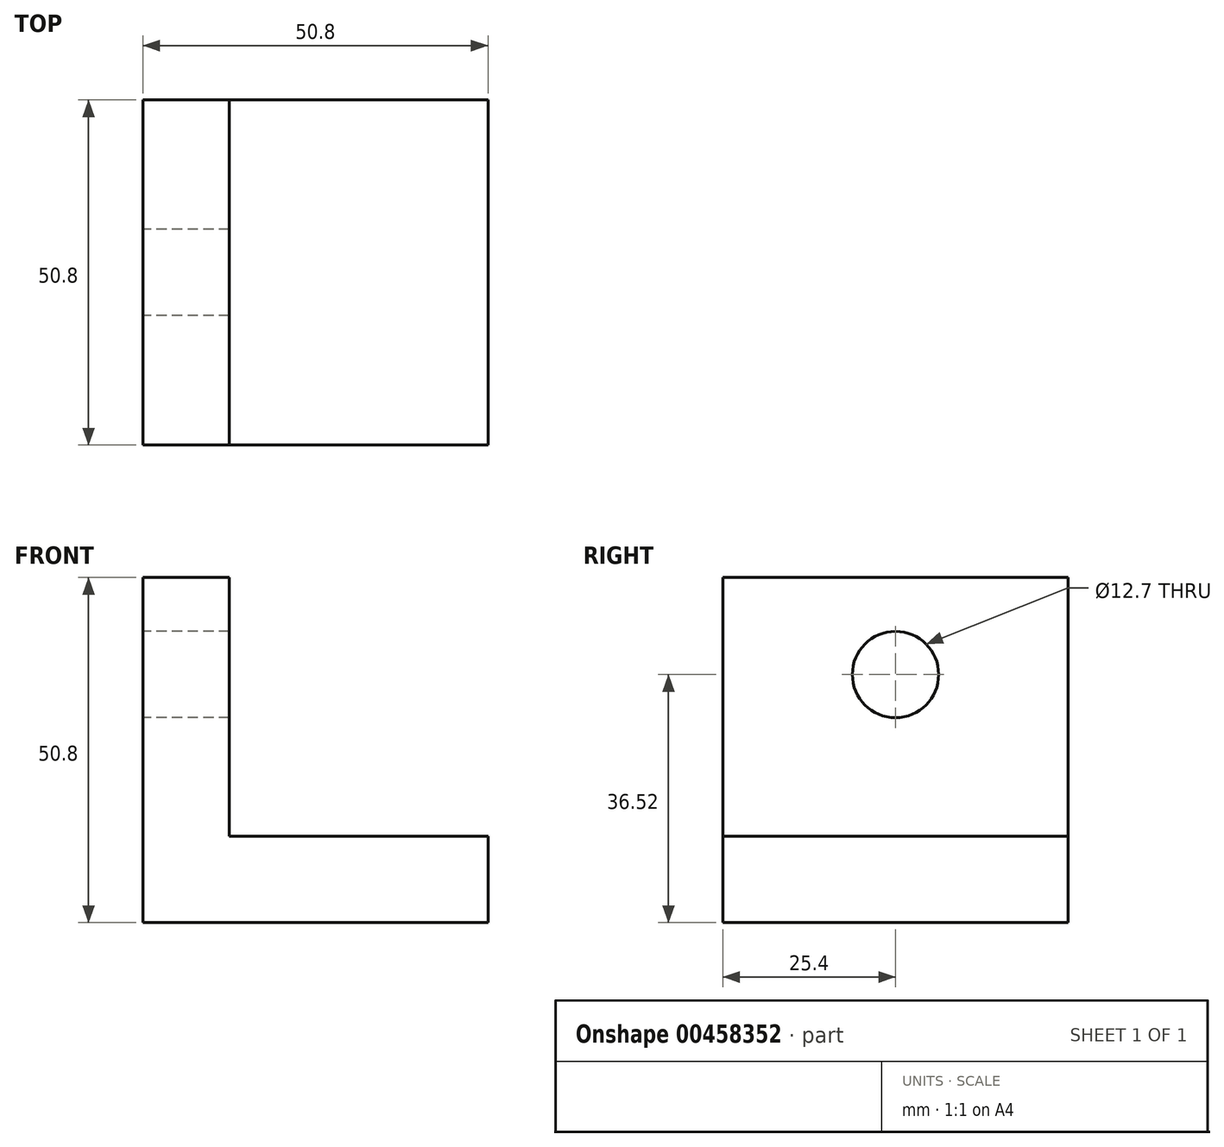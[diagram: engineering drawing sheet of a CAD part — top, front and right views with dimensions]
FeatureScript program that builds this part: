
annotation { "Feature Type Name" : "Feature", "Feature Type Description" : "" }
export const myFeature = defineFeature(function(context is Context, id is Id, definition is map)
    precondition{}
    {
        {
            var Q0;
            Q0=qCreatedBy(makeId("Right.planeOp"),FACE);
            var sketch = newSketch(context, id + "F0", { "sketchPlane" : qUnion([Q0])});
            skLineSegment(sketch, "E0", {"start": v(0, 0) * mm, "end": v(50.8, 0) * mm});
            skLineSegment(sketch, "E1", {"start": v(50.8, 0) * mm, "end": v(50.8, 50.8) * mm});
            skLineSegment(sketch, "E2", {"start": v(50.8, 50.8) * mm, "end": v(0, 50.8) * mm});
            skLineSegment(sketch, "E3", {"start": v(0, 50.8) * mm, "end": v(0, 0) * mm});
            skSolve(sketch);
        }
        {
            var Q0;
            Q0=qCreatedBy(makeId("Right.planeOp"),FACE);
            var sketch = newSketch(context, id + "F1", { "sketchPlane" : qUnion([Q0])});
            skLineSegment(sketch, "E4", {"start": v(0, 0) * mm, "end": v(0, 12.7) * mm});
            skLineSegment(sketch, "E5", {"start": v(0, 12.7) * mm, "end": v(50.8, 12.7) * mm});
            skLineSegment(sketch, "E6", {"start": v(50.8, 12.7) * mm, "end": v(50.8, 0) * mm});
            skLineSegment(sketch, "E7", {"start": v(50.8, 0) * mm, "end": v(0, 0) * mm});
            skSolve(sketch);
        }
        {
            var Q0;
            Q0=qCreatedBy(makeId("Right.planeOp"),FACE);
            var sketch = newSketch(context, id + "F2", { "sketchPlane" : qUnion([Q0])});
            skCircle(sketch, "E8", {"center": v(25.4, 36.52) * mm, "radius": 6.35 * mm});
            skSolve(sketch);
        }
        {
            var Q0;
            Q0 = qSketchRegion(id + "F0", true);
            extrude(context, id + "F3", {"entities" : qUnion([Q0]), "depth" : 12.7 * mm});
        }
        {
            var Q0;
            Q0 = qSketchRegion(id + "F1", true);
            extrude(context, id + "F4", {"entities" : qUnion([Q0]), "operationType" : NewBodyOperationType.ADD, "depth" : 50.8 * mm});
        }
        {
            var Q0;
            Q0 = qSketchRegion(id + "F2", true);
            extrude(context, id + "F5", {"entities" : qUnion([Q0]), "operationType" : NewBodyOperationType.REMOVE, "depth" : 48 * mm});
        }
    });
